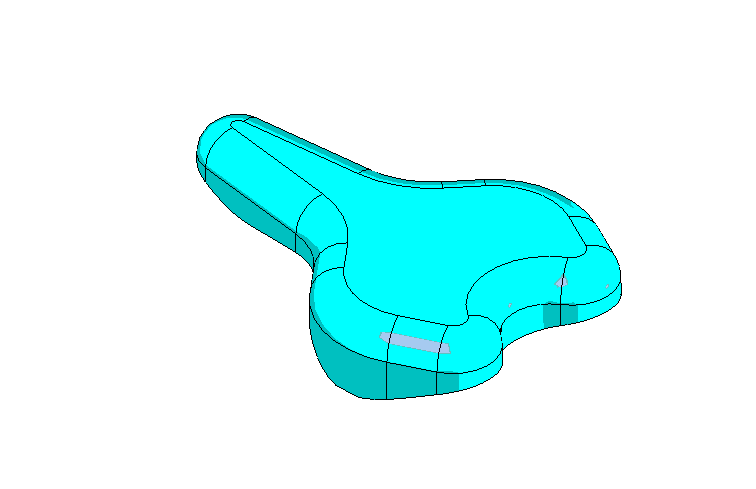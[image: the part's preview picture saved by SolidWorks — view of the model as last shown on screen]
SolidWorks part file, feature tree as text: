
SOLIDWORKS PART (.sldprt)
format: sldprt  version: not decoded by parser v0  size: 862,720 bytes
history: native  units: mm
features: sketch x7, plane x4, cut_extrude x3, fillet x3, extrude x2, revolve x2, material x1, mirror x1 (+10 scaffold rows collapsed)
feature tree (33):
  scaffold x10  (default folders/planes/origin — collapsed)
  material  "Matériau <non spécifié>"
  plane  "Plan de face"
  plane  "Plan de dessus"
  plane  "Plan de droite"
  sketch  "Esquisse1"  dims[c1.D1=49.0mm c1.D2=50.0mm c1.D5=134.0mm c1.D8=58.0mm c1.D9=29.0mm c1.D10=24.5mm c1.D3=168.0mm c1.D4=76.0mm c1.D6=57.0mm c1.D7=182.0mm c2.D8=73.0mm c2.D10=253.0mm c2.D11=98.0mm]
  extrude  "Extrusion1"  Depth=51mm
  sketch  "Esquisse2"  dims[D1=20.0mm D2=50.0mm D3=38.0mm D4=200.0mm D5=110.0mm D6=33.0mm D7=80.0mm D8=36.0mm D9=155.0mm D10=235.0mm D11=47.0mm D12=33.0mm]
  cut_extrude  "Enlèv. mat.-Extru.2"  [1 undecoded]
  fillet  "Congé1"  Radius=20mm
  sketch  "Esquisse3"  dims[D1=10.0mm]
  cut_extrude  "Enlèv. mat.-Extru.3"  [1 undecoded]
  fillet  "Congé2"  Radius=5mm
  sketch  "Esquisse4"  dims[c1.D1=7.0mm c1.D2=3.0mm c1.D3=12.0mm c1.D4=~21.624636mm c2.D4=90.0deg c3.D4=10.0mm]
  extrude  "Extrusion2"  [1 undecoded]
  plane  "Plan1"  Offset=52mm
  sketch  "Esquisse5"  dims[D1=200.0mm D2=15.0mm D3=18.0mm]
  revolve  "Révolution1"  Angle=360deg
  sketch  "Esquisse6"  dims[c1.D1=14.0mm c1.D2=~68.965975mm c2.D2=30.0deg c2.D3=180.0mm c2.D4=26.0mm c3.D2=6.0mm]
  revolve  "Révolution2"  Angle=360deg
  sketch  "Esquisse7"  dims[D1=7.0mm]
  cut_extrude  "Enlèv. mat.-Extru.4"  Depth=20mm
  fillet  "Congé3"  Radius=2mm
  mirror  "Symétrie1"
decode coverage: 14 of 18 modeling features carry decoded parameters
note: ~ marks probable driven/reference dimensions
note: 3 parameter values undecoded
summary: no parameter record found for 3 features
note: suppression state not decoded; provenance and decode notes live in map.json
